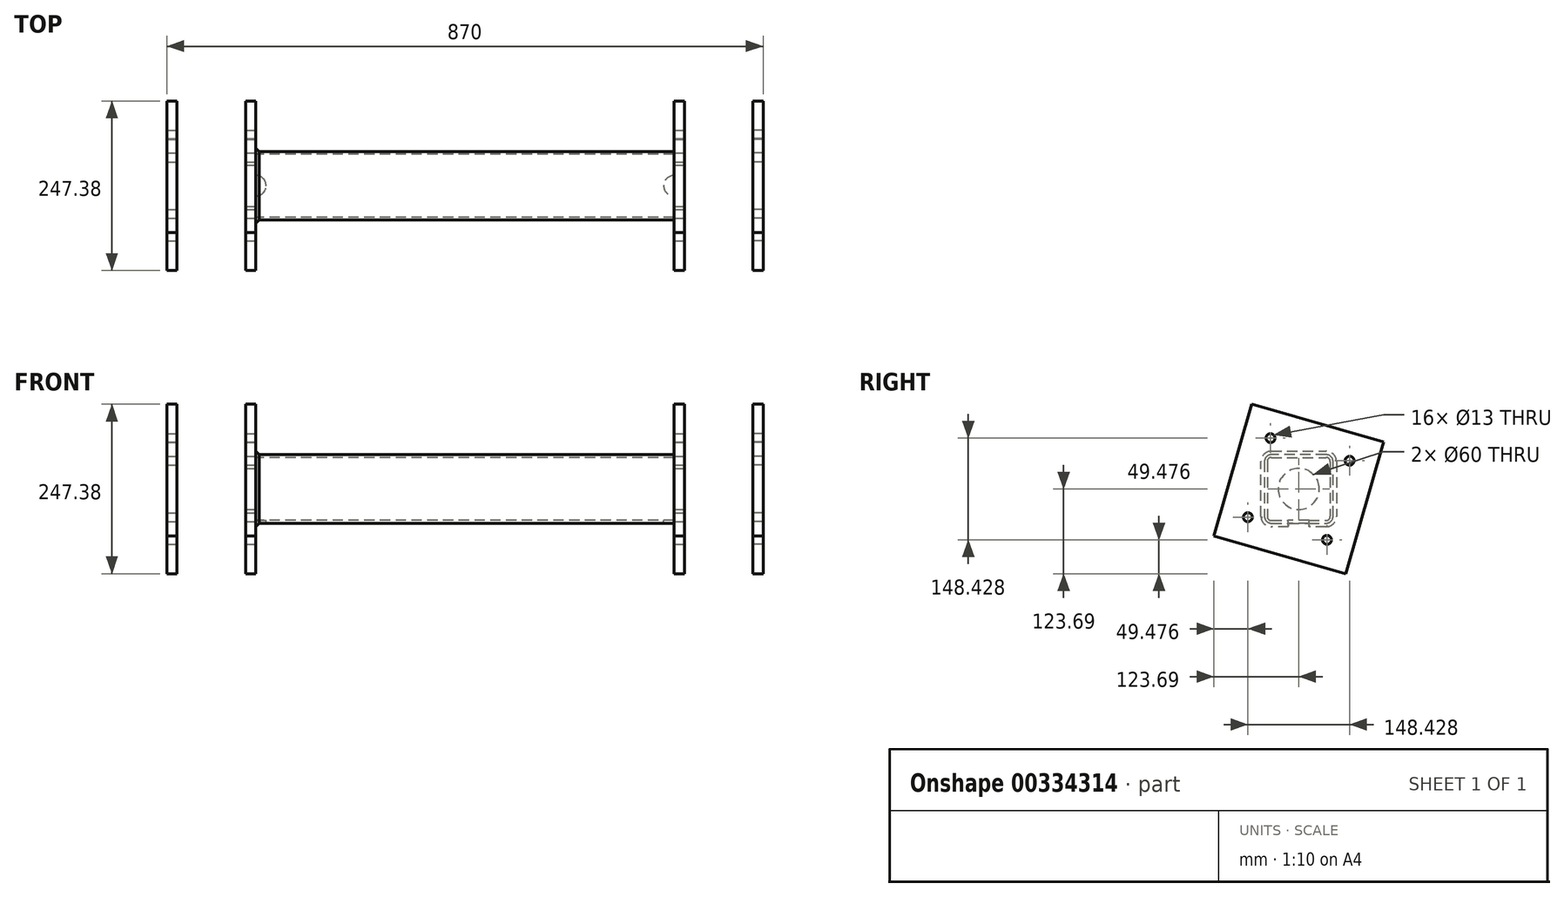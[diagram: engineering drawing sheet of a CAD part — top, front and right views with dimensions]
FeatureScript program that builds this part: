
annotation { "Feature Type Name" : "Feature", "Feature Type Description" : "" }
export const myFeature = defineFeature(function(context is Context, id is Id, definition is map)
    precondition{}
    {
        {
            var Q0;
            Q0=qCreatedBy(makeId("Right.planeOp"),FACE);
            var sketch = newSketch(context, id + "F0", { "sketchPlane" : qUnion([Q0])});
            skLineSegment(sketch, "E0.bottom", {"start": v(-40, 50) * mm, "end": v(40, 50) * mm});
            skLineSegment(sketch, "E0.top", {"start": v(-40, -50) * mm, "end": v(40, -50) * mm});
            skLineSegment(sketch, "E0.left", {"start": v(-50, 40) * mm, "end": v(-50, -40) * mm});
            skLineSegment(sketch, "E0.right", {"start": v(50, 40) * mm, "end": v(50, -40) * mm});
            skPoint(sketch, "E0.middle", {"position": v(0, 0) * mm});
            skPoint(sketch, "E1.visualSharp", {"position": v(50, 50) * mm});
            skArc(sketch, "E1.filletArc", {"start": v(50, 40) * mm, "mid": v(47.07, 47.07) * mm, "end": v(40, 50) * mm});
            skPoint(sketch, "E2.visualSharp", {"position": v(-50, 50) * mm});
            skArc(sketch, "E2.filletArc", {"start": v(-40, 50) * mm, "mid": v(-47.07, 47.07) * mm, "end": v(-50, 40) * mm});
            skPoint(sketch, "E3.visualSharp", {"position": v(-50, -50) * mm});
            skArc(sketch, "E3.filletArc", {"start": v(-50, -40) * mm, "mid": v(-47.07, -47.07) * mm, "end": v(-40, -50) * mm});
            skPoint(sketch, "E4.visualSharp", {"position": v(50, -50) * mm});
            skArc(sketch, "E4.filletArc", {"start": v(40, -50) * mm, "mid": v(47.07, -47.07) * mm, "end": v(50, -40) * mm});
            skArc(sketch, "E5.0", {"start": v(-40, 46) * mm, "mid": v(-44.24, 44.24) * mm, "end": v(-46, 40) * mm});
            skLineSegment(sketch, "E5.1", {"start": v(-46, 40) * mm, "end": v(-46, -40) * mm});
            skLineSegment(sketch, "E5.2", {"start": v(-40, 46) * mm, "end": v(40, 46) * mm});
            skArc(sketch, "E5.3", {"start": v(-46, -40) * mm, "mid": v(-44.24, -44.24) * mm, "end": v(-40, -46) * mm});
            skArc(sketch, "E5.4", {"start": v(46, 40) * mm, "mid": v(44.24, 44.24) * mm, "end": v(40, 46) * mm});
            skLineSegment(sketch, "E5.5", {"start": v(46, 40) * mm, "end": v(46, -40) * mm});
            skArc(sketch, "E5.6", {"start": v(40, -46) * mm, "mid": v(44.24, -44.24) * mm, "end": v(46, -40) * mm});
            skLineSegment(sketch, "E5.7", {"start": v(-40, -46) * mm, "end": v(40, -46) * mm});
            skSolve(sketch);
        }
        {
            var Q0;
            Q0=makeQuery(id+"F0.imprint","IMPRINT",FACE,{"disambiguationData":[TD([[makeQuery(id+"F0.imprint","IMPRINT",EDGE,{"derivedFrom":sQuery(id+"F0.wireOp",EDGE,"E0.bottom")}),-1.0]])]});
            extrude(context, id + "F1", {"entities" : qUnion([Q0]), "depth" : 640 * mm});
        }
        {
            var Q0;
            Q0=makeQuery(id+"F1.opExtrude","CAP_FACE",FACE,{"disambiguationData":[OSD([sQuery(id+"F0.wireOp",EDGE,"E0.bottom"),sQuery(id+"F0.wireOp",EDGE,"E0.top"),sQuery(id+"F0.wireOp",EDGE,"E0.left"),sQuery(id+"F0.wireOp",EDGE,"E0.right"),sQuery(id+"F0.wireOp",EDGE,"E1.filletArc"),sQuery(id+"F0.wireOp",EDGE,"E2.filletArc"),sQuery(id+"F0.wireOp",EDGE,"E3.filletArc"),sQuery(id+"F0.wireOp",EDGE,"E4.filletArc"),sQuery(id+"F0.wireOp",EDGE,"E5.0"),sQuery(id+"F0.wireOp",EDGE,"E5.1"),sQuery(id+"F0.wireOp",EDGE,"E5.2"),sQuery(id+"F0.wireOp",EDGE,"E5.3"),sQuery(id+"F0.wireOp",EDGE,"E5.4"),sQuery(id+"F0.wireOp",EDGE,"E5.5"),sQuery(id+"F0.wireOp",EDGE,"E5.6"),sQuery(id+"F0.wireOp",EDGE,"E5.7")])],"isStart":false});
            var sketch = newSketch(context, id + "F2", { "sketchPlane" : qUnion([Q0])});
            skLineSegment(sketch, "E6", {"start": v(-75.17, 21.6) * mm, "end": v(117.08, -33.54) * mm, "construction": true});
            skLineSegment(sketch, "E7", {"start": v(-63.23, 0) * mm, "end": v(69.28, 0) * mm, "construction": true});
            skPoint(sketch, "E7.endSnap0", {"position": v(46, 0) * mm});
            skLineSegment(sketch, "E8.bottom", {"start": v(123.69, 68.56) * mm, "end": v(-68.56, 123.69) * mm});
            skLineSegment(sketch, "E8.top", {"start": v(68.56, -123.69) * mm, "end": v(-123.69, -68.56) * mm});
            skLineSegment(sketch, "E8.left", {"start": v(123.69, 68.56) * mm, "end": v(68.56, -123.69) * mm});
            skLineSegment(sketch, "E8.right", {"start": v(-68.56, 123.69) * mm, "end": v(-123.69, -68.56) * mm});
            skPoint(sketch, "E8.middle", {"position": v(0, 0) * mm});
            skLineSegment(sketch, "E9.0", {"start": v(74.21, 41.14) * mm, "end": v(-41.14, 74.21) * mm, "construction": true});
            skLineSegment(sketch, "E9.1", {"start": v(74.21, 41.14) * mm, "end": v(41.14, -74.21) * mm, "construction": true});
            skLineSegment(sketch, "E9.2", {"start": v(41.14, -74.21) * mm, "end": v(-74.21, -41.14) * mm, "construction": true});
            skLineSegment(sketch, "E9.3", {"start": v(-41.14, 74.21) * mm, "end": v(-74.21, -41.14) * mm, "construction": true});
            skCircle(sketch, "E10", {"center": v(-41.14, 74.21) * mm, "radius": 6.5 * mm});
            skCircle(sketch, "E11", {"center": v(74.21, 41.14) * mm, "radius": 6.5 * mm});
            skCircle(sketch, "E12", {"center": v(41.14, -74.21) * mm, "radius": 6.5 * mm});
            skCircle(sketch, "E13", {"center": v(-74.21, -41.14) * mm, "radius": 6.5 * mm});
            skLineSegment(sketch, "E14.bottom", {"start": v(35, 35) * mm, "end": v(-35, 35) * mm, "construction": true});
            skLineSegment(sketch, "E14.top", {"start": v(35, -35) * mm, "end": v(-35, -35) * mm, "construction": true});
            skLineSegment(sketch, "E14.left", {"start": v(35, 35) * mm, "end": v(35, -35) * mm, "construction": true});
            skLineSegment(sketch, "E14.right", {"start": v(-35, 35) * mm, "end": v(-35, -35) * mm, "construction": true});
            skCircle(sketch, "E15", {"center": v(35, 35) * mm, "radius": 6.5 * mm, "construction": true});
            skCircle(sketch, "E16", {"center": v(-35, -35) * mm, "radius": 6.5 * mm, "construction": true});
            skCircle(sketch, "E17", {"center": v(0, 0) * mm, "radius": 30 * mm});
            skSolve(sketch);
        }
        {
            var Q0;
            Q0=makeQuery(id+"F2.imprint","IMPRINT",FACE,{"disambiguationData":[TD([[makeQuery(id+"F2.imprint","IMPRINT",EDGE,{"derivedFrom":sQuery(id+"F2.wireOp",EDGE,"E8.bottom")}),1.0]])]});
            var Q1;
            Q1=makeQuery(id+"F2.imprint","IMPRINT",FACE,{"disambiguationData":[TD([[makeQuery(id+"F2.imprint","IMPRINT",EDGE,{"derivedFrom":makeQuery(id+"F1.opExtrude","CAP_EDGE",EDGE,{"disambiguationData":[OSD([sQuery(id+"F0.wireOp",EDGE,"E5.0")])],"isStart":false})}),1.0]])]});
            extrude(context, id + "F3", {"entities" : qUnion([Q0, Q1]), "operationType" : NewBodyOperationType.ADD, "oppositeDirection" : true, "depth" : 15 * mm});
        }
        {
            var Q0;
            Q0=qSketchRegion(id+"F2",true);
            extrude(context, id + "F4", {"entities" : qUnion([Q0]), "operationType" : NewBodyOperationType.ADD, "oppositeDirection" : true, "depth" : 640 * mm, "hasSecondDirection" : true, "secondDirectionOppositeDirection" : true, "secondDirectionDepth" : (640 - 15) * mm});
        }
        {
            var Q0;
            Q0=makeQuery(id+"F3.opExtrude","CAP_EDGE",EDGE,{"disambiguationData":[OSD([sQuery(id+"F0.wireOp",EDGE,"E0.bottom")])],"isStart":false});
            var Q1;
            Q1=makeQuery(id+"F3.opExtrude","CAP_EDGE",EDGE,{"disambiguationData":[OSD([sQuery(id+"F0.wireOp",EDGE,"E1.filletArc")])],"isStart":false});
            var Q2;
            Q2=makeQuery(id+"F3.opExtrude","CAP_EDGE",EDGE,{"disambiguationData":[OSD([sQuery(id+"F0.wireOp",EDGE,"E0.right")])],"isStart":false});
            var Q3;
            Q3=makeQuery(id+"F3.opExtrude","CAP_EDGE",EDGE,{"disambiguationData":[OSD([sQuery(id+"F0.wireOp",EDGE,"E4.filletArc")])],"isStart":false});
            var Q4;
            Q4=makeQuery(id+"F3.opExtrude","CAP_EDGE",EDGE,{"disambiguationData":[OSD([sQuery(id+"F0.wireOp",EDGE,"E2.filletArc")])],"isStart":false});
            var Q5;
            Q5=makeQuery(id+"F3.opExtrude","CAP_EDGE",EDGE,{"disambiguationData":[OSD([sQuery(id+"F0.wireOp",EDGE,"E0.left")])],"isStart":false});
            var Q6;
            Q6=makeQuery(id+"F3.opExtrude","CAP_EDGE",EDGE,{"disambiguationData":[OSD([sQuery(id+"F0.wireOp",EDGE,"E3.filletArc")])],"isStart":false});
            var Q7;
            Q7=makeQuery(id+"F3.opExtrude","CAP_EDGE",EDGE,{"disambiguationData":[OSD([sQuery(id+"F0.wireOp",EDGE,"E0.top")])],"isStart":false});
            var Q8;
            Q8=makeQuery(id+"F4.boolean.opBoolean","INTERSECT",EDGE,{"derivedFrom":[makeQuery(id+"F1.opExtrude","SWEPT_FACE",FACE,{"disambiguationData":[OSD([sQuery(id+"F0.wireOp",EDGE,"E0.left")])]}),makeQuery(id+"F4.opExtrude","CAP_FACE",FACE,{"disambiguationData":[OSD([sQuery(id+"F2.wireOp",EDGE,"E8.bottom"),sQuery(id+"F2.wireOp",EDGE,"E8.top"),sQuery(id+"F2.wireOp",EDGE,"E8.left"),sQuery(id+"F2.wireOp",EDGE,"E8.right"),sQuery(id+"F2.wireOp",EDGE,"E10"),sQuery(id+"F2.wireOp",EDGE,"E11"),sQuery(id+"F2.wireOp",EDGE,"E12"),sQuery(id+"F2.wireOp",EDGE,"E13")])],"isStart":true})]});
            var Q9;
            Q9=makeQuery(id+"F4.boolean.opBoolean","INTERSECT",EDGE,{"derivedFrom":[makeQuery(id+"F1.opExtrude","SWEPT_FACE",FACE,{"disambiguationData":[OSD([sQuery(id+"F0.wireOp",EDGE,"E2.filletArc")])]}),makeQuery(id+"F4.opExtrude","CAP_FACE",FACE,{"disambiguationData":[OSD([sQuery(id+"F2.wireOp",EDGE,"E8.bottom"),sQuery(id+"F2.wireOp",EDGE,"E8.top"),sQuery(id+"F2.wireOp",EDGE,"E8.left"),sQuery(id+"F2.wireOp",EDGE,"E8.right"),sQuery(id+"F2.wireOp",EDGE,"E10"),sQuery(id+"F2.wireOp",EDGE,"E11"),sQuery(id+"F2.wireOp",EDGE,"E12"),sQuery(id+"F2.wireOp",EDGE,"E13")])],"isStart":true})]});
            var Q10;
            Q10=makeQuery(id+"F4.boolean.opBoolean","INTERSECT",EDGE,{"derivedFrom":[makeQuery(id+"F1.opExtrude","SWEPT_FACE",FACE,{"disambiguationData":[OSD([sQuery(id+"F0.wireOp",EDGE,"E3.filletArc")])]}),makeQuery(id+"F4.opExtrude","CAP_FACE",FACE,{"disambiguationData":[OSD([sQuery(id+"F2.wireOp",EDGE,"E8.bottom"),sQuery(id+"F2.wireOp",EDGE,"E8.top"),sQuery(id+"F2.wireOp",EDGE,"E8.left"),sQuery(id+"F2.wireOp",EDGE,"E8.right"),sQuery(id+"F2.wireOp",EDGE,"E10"),sQuery(id+"F2.wireOp",EDGE,"E11"),sQuery(id+"F2.wireOp",EDGE,"E12"),sQuery(id+"F2.wireOp",EDGE,"E13")])],"isStart":true})]});
            var Q11;
            Q11=makeQuery(id+"F4.boolean.opBoolean","INTERSECT",EDGE,{"derivedFrom":[makeQuery(id+"F1.opExtrude","SWEPT_FACE",FACE,{"disambiguationData":[OSD([sQuery(id+"F0.wireOp",EDGE,"E0.top")])]}),makeQuery(id+"F4.opExtrude","CAP_FACE",FACE,{"disambiguationData":[OSD([sQuery(id+"F2.wireOp",EDGE,"E8.bottom"),sQuery(id+"F2.wireOp",EDGE,"E8.top"),sQuery(id+"F2.wireOp",EDGE,"E8.left"),sQuery(id+"F2.wireOp",EDGE,"E8.right"),sQuery(id+"F2.wireOp",EDGE,"E10"),sQuery(id+"F2.wireOp",EDGE,"E11"),sQuery(id+"F2.wireOp",EDGE,"E12"),sQuery(id+"F2.wireOp",EDGE,"E13")])],"isStart":true})]});
            var Q12;
            Q12=makeQuery(id+"F4.boolean.opBoolean","INTERSECT",EDGE,{"derivedFrom":[makeQuery(id+"F1.opExtrude","SWEPT_FACE",FACE,{"disambiguationData":[OSD([sQuery(id+"F0.wireOp",EDGE,"E4.filletArc")])]}),makeQuery(id+"F4.opExtrude","CAP_FACE",FACE,{"disambiguationData":[OSD([sQuery(id+"F2.wireOp",EDGE,"E8.bottom"),sQuery(id+"F2.wireOp",EDGE,"E8.top"),sQuery(id+"F2.wireOp",EDGE,"E8.left"),sQuery(id+"F2.wireOp",EDGE,"E8.right"),sQuery(id+"F2.wireOp",EDGE,"E10"),sQuery(id+"F2.wireOp",EDGE,"E11"),sQuery(id+"F2.wireOp",EDGE,"E12"),sQuery(id+"F2.wireOp",EDGE,"E13")])],"isStart":true})]});
            var Q13;
            Q13=makeQuery(id+"F4.boolean.opBoolean","INTERSECT",EDGE,{"derivedFrom":[makeQuery(id+"F1.opExtrude","SWEPT_FACE",FACE,{"disambiguationData":[OSD([sQuery(id+"F0.wireOp",EDGE,"E0.right")])]}),makeQuery(id+"F4.opExtrude","CAP_FACE",FACE,{"disambiguationData":[OSD([sQuery(id+"F2.wireOp",EDGE,"E8.bottom"),sQuery(id+"F2.wireOp",EDGE,"E8.top"),sQuery(id+"F2.wireOp",EDGE,"E8.left"),sQuery(id+"F2.wireOp",EDGE,"E8.right"),sQuery(id+"F2.wireOp",EDGE,"E10"),sQuery(id+"F2.wireOp",EDGE,"E11"),sQuery(id+"F2.wireOp",EDGE,"E12"),sQuery(id+"F2.wireOp",EDGE,"E13")])],"isStart":true})]});
            var Q14;
            Q14=makeQuery(id+"F4.boolean.opBoolean","INTERSECT",EDGE,{"derivedFrom":[makeQuery(id+"F1.opExtrude","SWEPT_FACE",FACE,{"disambiguationData":[OSD([sQuery(id+"F0.wireOp",EDGE,"E1.filletArc")])]}),makeQuery(id+"F4.opExtrude","CAP_FACE",FACE,{"disambiguationData":[OSD([sQuery(id+"F2.wireOp",EDGE,"E8.bottom"),sQuery(id+"F2.wireOp",EDGE,"E8.top"),sQuery(id+"F2.wireOp",EDGE,"E8.left"),sQuery(id+"F2.wireOp",EDGE,"E8.right"),sQuery(id+"F2.wireOp",EDGE,"E10"),sQuery(id+"F2.wireOp",EDGE,"E11"),sQuery(id+"F2.wireOp",EDGE,"E12"),sQuery(id+"F2.wireOp",EDGE,"E13")])],"isStart":true})]});
            var Q15;
            Q15=makeQuery(id+"F4.boolean.opBoolean","INTERSECT",EDGE,{"derivedFrom":[makeQuery(id+"F1.opExtrude","SWEPT_FACE",FACE,{"disambiguationData":[OSD([sQuery(id+"F0.wireOp",EDGE,"E0.bottom")])]}),makeQuery(id+"F4.opExtrude","CAP_FACE",FACE,{"disambiguationData":[OSD([sQuery(id+"F2.wireOp",EDGE,"E8.bottom"),sQuery(id+"F2.wireOp",EDGE,"E8.top"),sQuery(id+"F2.wireOp",EDGE,"E8.left"),sQuery(id+"F2.wireOp",EDGE,"E8.right"),sQuery(id+"F2.wireOp",EDGE,"E10"),sQuery(id+"F2.wireOp",EDGE,"E11"),sQuery(id+"F2.wireOp",EDGE,"E12"),sQuery(id+"F2.wireOp",EDGE,"E13")])],"isStart":true})]});
            chamfer(context, id + "F5", {"entities" : qUnion([Q0, Q1, Q2, Q3, Q4, Q5, Q6, Q7, Q8, Q9, Q10, Q11, Q12, Q13, Q14, Q15]), "width" : 5 * mm, "tangentPropagation" : true});
        }
        {
            var Q0;
            Q0=makeQuery(id+"F1.opExtrude","SWEPT_FACE",FACE,{"disambiguationData":[OSD([sQuery(id+"F0.wireOp",EDGE,"E0.top")])]});
            var sketch = newSketch(context, id + "F6", { "sketchPlane" : qUnion([Q0])});
            skLineSegment(sketch, "E18.0", {"start": v(625, 40) * mm, "end": v(625, -40) * mm, "construction": true});
            skLineSegment(sketch, "E19.0", {"start": v(15, -40) * mm, "end": v(15, 40) * mm, "construction": true});
            skArc(sketch, "E20", {"start": v(15, 15) * mm, "mid": v(30, 0) * mm, "end": v(15, -15) * mm});
            skLineSegment(sketch, "E21", {"start": v(15, 15) * mm, "end": v(15, -15) * mm});
            skArc(sketch, "E22", {"start": v(625, -15) * mm, "mid": v(610, 0) * mm, "end": v(625, 15) * mm});
            skLineSegment(sketch, "E23", {"start": v(625, 15) * mm, "end": v(625, -15) * mm});
            skSolve(sketch);
        }
        {
            var Q0;
            Q0=qSketchRegion(id+"F6",true);
            extrude(context, id + "F7", {"entities" : qUnion([Q0]), "operationType" : NewBodyOperationType.REMOVE, "depth" : 50 * mm, "symmetric" : true});
        }
        {
            var Q0;
            Q0=qSketchRegion(id+"F2",true);
            var Q1;
            Q1=makeQuery(id+"F2.imprint","IMPRINT",FACE,{"disambiguationData":[TD([[makeQuery(id+"F2.imprint","IMPRINT",EDGE,{"derivedFrom":sQuery(id+"F2.wireOp",EDGE,"E17")}),1.0]])]});
            extrude(context, id + "F8", {"entities" : qUnion([Q0, Q1]), "depth" : 115 * mm, "hasSecondDirection" : true, "secondDirectionOppositeDirection" : false, "secondDirectionDepth" : 100 * mm});
        }
        {
            var Q0;
            Q0=qSketchRegion(id+"F2",true);
            var Q1;
            Q1=makeQuery(id+"F2.imprint","IMPRINT",FACE,{"disambiguationData":[TD([[makeQuery(id+"F2.imprint","IMPRINT",EDGE,{"derivedFrom":sQuery(id+"F2.wireOp",EDGE,"E17")}),1.0]])]});
            extrude(context, id + "F9", {"entities" : qUnion([Q0, Q1]), "oppositeDirection" : true, "depth" : 755 * mm, "hasSecondDirection" : true, "secondDirectionOppositeDirection" : true, "secondDirectionDepth" : 740 * mm});
        }
    });
